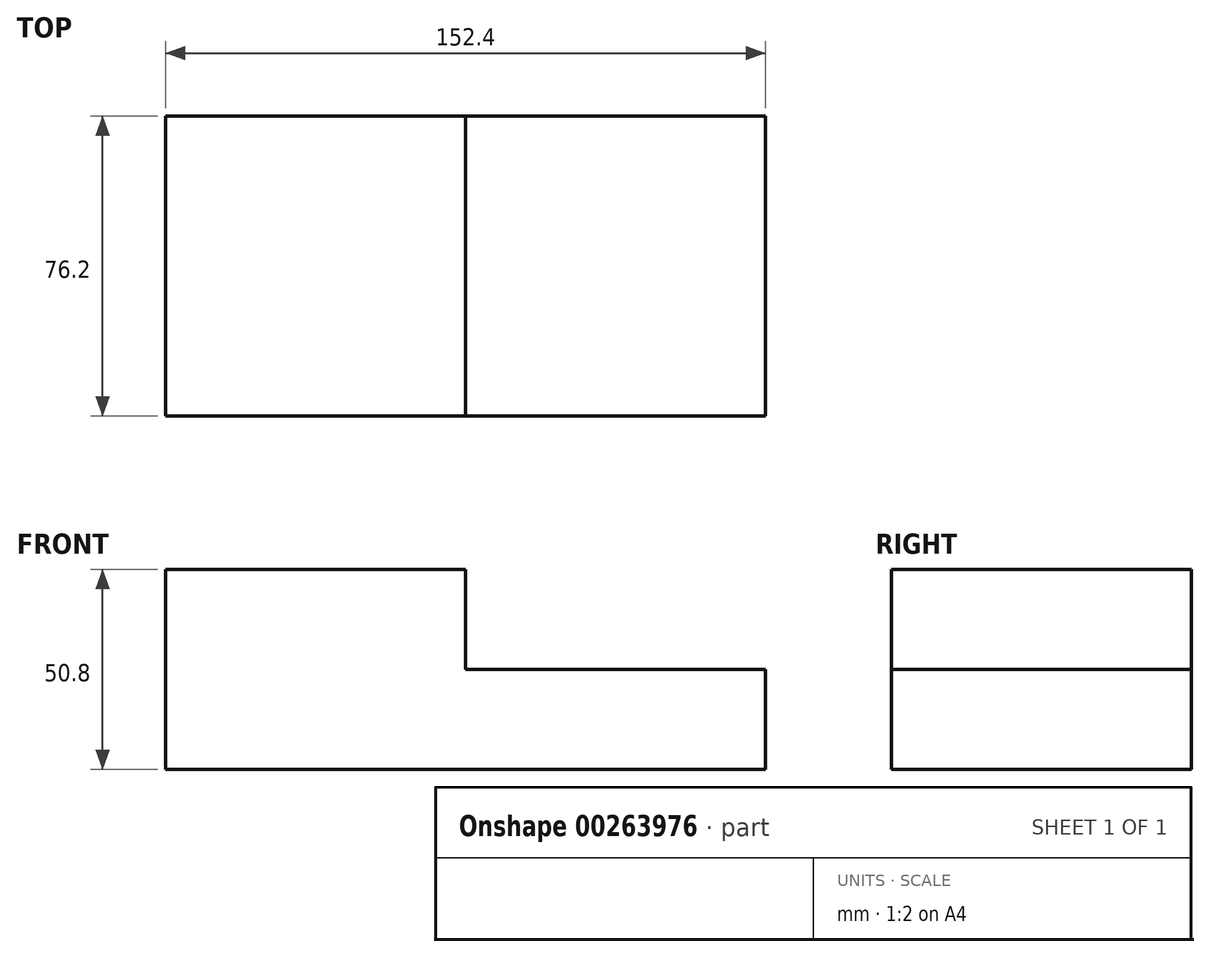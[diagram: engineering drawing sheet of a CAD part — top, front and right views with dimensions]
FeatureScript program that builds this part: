
annotation { "Feature Type Name" : "Feature", "Feature Type Description" : "" }
export const myFeature = defineFeature(function(context is Context, id is Id, definition is map)
    precondition{}
    {
        {
            var Q0;
            Q0=qCreatedBy(makeId("Front.planeOp"),FACE);
            var sketch = newSketch(context, id + "F0", { "sketchPlane" : qUnion([Q0])});
            skLineSegment(sketch, "E0", {"start": v(76.2, 0) * mm, "end": v(-76.2, 0) * mm});
            skLineSegment(sketch, "E1", {"start": v(-76.2, 0) * mm, "end": v(-76.2, 50.8) * mm});
            skLineSegment(sketch, "E2", {"start": v(-76.2, 50.8) * mm, "end": v(0, 50.8) * mm});
            skLineSegment(sketch, "E3", {"start": v(0, 50.8) * mm, "end": v(0, 25.4) * mm});
            skLineSegment(sketch, "E4", {"start": v(0, 25.4) * mm, "end": v(76.2, 25.4) * mm});
            skLineSegment(sketch, "E5", {"start": v(76.2, 25.4) * mm, "end": v(76.2, 0) * mm});
            skSolve(sketch);
        }
        {
            var Q0;
            Q0=makeQuery(id+"F0.imprint","IMPRINT",FACE,{"disambiguationData":[TD([[makeQuery(id+"F0.imprint","IMPRINT",EDGE,{"derivedFrom":sQuery(id+"F0.wireOp",EDGE,"E0")}),-1.0]])]});
            extrude(context, id + "F1", {"entities" : qUnion([Q0]), "oppositeDirection" : true, "depth" : 76.2 * mm});
        }
    });
